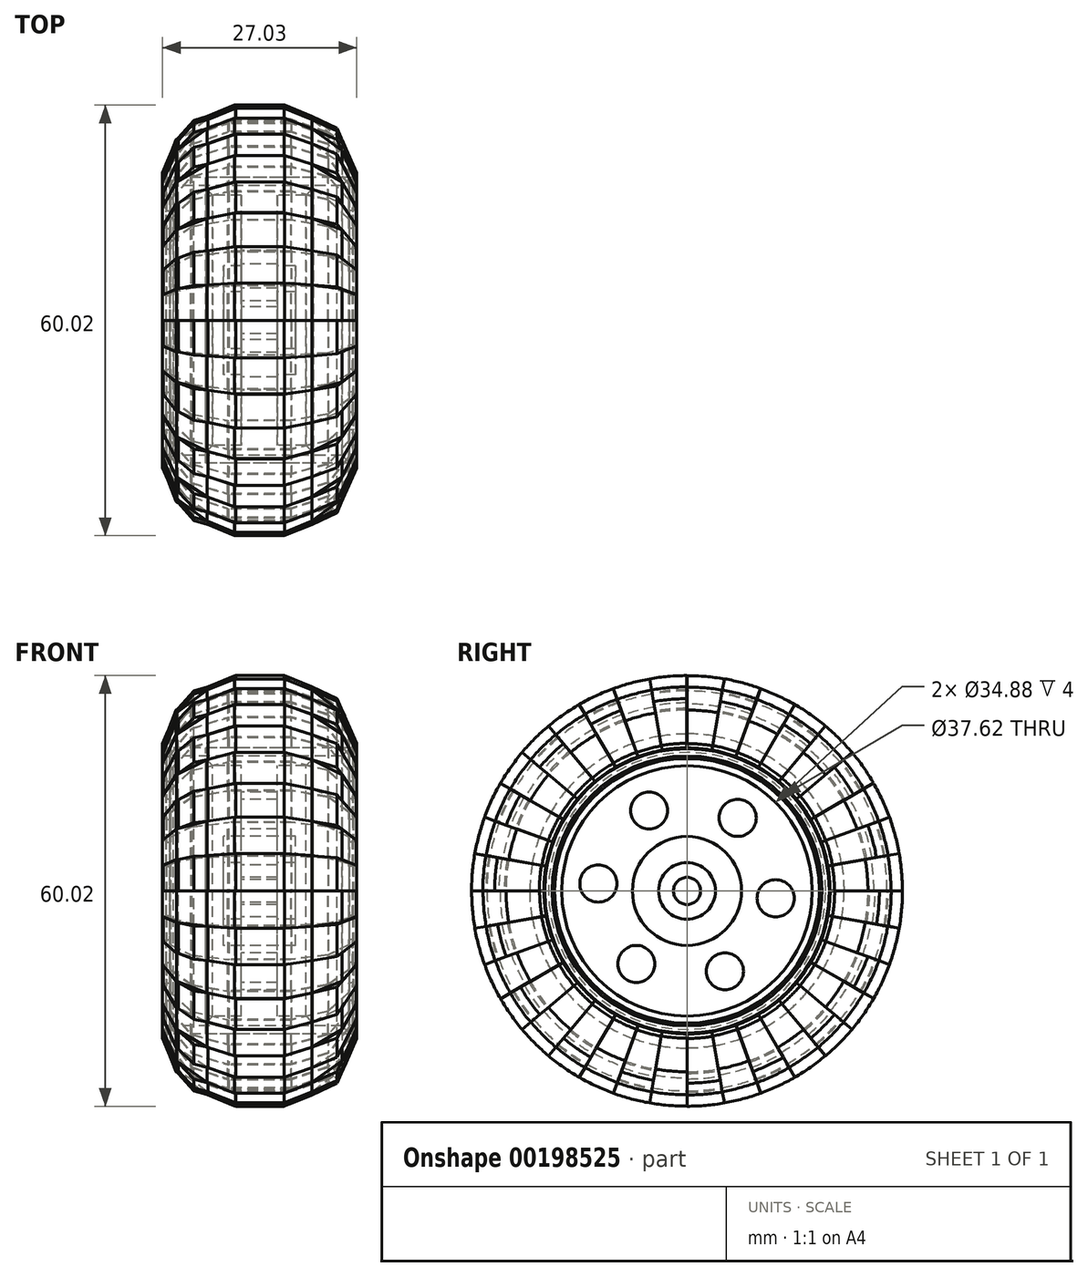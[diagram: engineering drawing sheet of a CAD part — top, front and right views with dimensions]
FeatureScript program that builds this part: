
annotation { "Feature Type Name" : "Feature", "Feature Type Description" : "" }
export const myFeature = defineFeature(function(context is Context, id is Id, definition is map)
    precondition{}
    {
        {
            var Q0;
            Q0=qCreatedBy(makeId("Top.planeOp"),FACE);
            var sketch = newSketch(context, id + "F0", { "sketchPlane" : qUnion([Q0])});
            skEllipse(sketch, "E0", {"center": v(0, -20) * mm, "majorRadius": 13.5 * mm, "minorRadius": 10 * mm, "majorAxis": v(1, 0), "construction": true});
            skLineSegment(sketch, "E1", {"start": v(0, 0) * mm, "end": v(0, -45.8) * mm, "construction": true});
            skLineSegment(sketch, "E2", {"start": v(-18.98, 0) * mm, "end": v(27.13, 0) * mm, "construction": true});
            skLineSegment(sketch, "E3", {"start": v(0, -30) * mm, "end": v(-3.5, -30) * mm});
            skLineSegment(sketch, "E4", {"start": v(-3.5, -30) * mm, "end": v(-7.3, -28.4) * mm});
            skLineSegment(sketch, "E5", {"start": v(-7.3, -28.4) * mm, "end": v(-11.53, -25.2) * mm});
            skLineSegment(sketch, "E6", {"start": v(-11.53, -25.2) * mm, "end": v(-11.53, -25.2) * mm});
            skLineSegment(sketch, "E7", {"start": v(-13, -20.54) * mm, "end": v(-13.01, -19.92) * mm});
            skLineSegment(sketch, "E8", {"start": v(-13.01, -19.92) * mm, "end": v(-12.45, -19.92) * mm});
            skLineSegment(sketch, "E9", {"start": v(-12.45, -19.92) * mm, "end": v(-12.45, -21.9) * mm});
            skLineSegment(sketch, "E10", {"start": v(-12.45, -21.9) * mm, "end": v(-9.59, -26.05) * mm});
            skLineSegment(sketch, "E11", {"start": v(-9.59, -26.05) * mm, "end": v(-4.45, -27.86) * mm});
            skLineSegment(sketch, "E12", {"start": v(-4.45, -27.86) * mm, "end": v(0, -27.86) * mm});
            skLineSegment(sketch, "E13", {"start": v(-11.53, -25.2) * mm, "end": v(-13.48, -20.53) * mm});
            skLineSegment(sketch, "E14", {"start": v(-13.48, -20.53) * mm, "end": v(-13, -20.54) * mm});
            skLineSegment(sketch, "E15.MirrorCS", {"start": v(13.48, -20.53) * mm, "end": v(13, -20.54) * mm});
            skLineSegment(sketch, "E16.MirrorCS", {"start": v(11.53, -25.2) * mm, "end": v(11.53, -25.2) * mm});
            skLineSegment(sketch, "E17.MirrorCS", {"start": v(3.5, -30) * mm, "end": v(7.3, -28.4) * mm});
            skLineSegment(sketch, "E18.MirrorCS", {"start": v(13.01, -19.92) * mm, "end": v(12.45, -19.92) * mm});
            skLineSegment(sketch, "E19.MirrorCS", {"start": v(4.45, -27.86) * mm, "end": v(0, -27.86) * mm});
            skLineSegment(sketch, "E20.MirrorCS", {"start": v(11.53, -25.2) * mm, "end": v(13.48, -20.53) * mm});
            skLineSegment(sketch, "E21.MirrorCS", {"start": v(9.59, -26.05) * mm, "end": v(4.45, -27.86) * mm});
            skLineSegment(sketch, "E22.MirrorCS", {"start": v(7.3, -28.4) * mm, "end": v(11.53, -25.2) * mm});
            skLineSegment(sketch, "E23.MirrorCS", {"start": v(0, -30) * mm, "end": v(3.5, -30) * mm});
            skLineSegment(sketch, "E24.MirrorCS", {"start": v(12.45, -21.9) * mm, "end": v(9.59, -26.05) * mm});
            skLineSegment(sketch, "E25.MirrorCS", {"start": v(12.45, -19.92) * mm, "end": v(12.45, -21.9) * mm});
            skLineSegment(sketch, "E26.MirrorCS", {"start": v(13, -20.54) * mm, "end": v(13.01, -19.92) * mm});
            skSolve(sketch);
        }
        {
            var Q0;
            Q0 = qSketchRegion(id + "F0", true);
            var Q1;
            Q1=sQuery(id+"F0.wireOp",EDGE,"E2");
            revolve(context, id + "F1", {"entities" : qUnion([Q0]), "axis" : qUnion([Q1]), "revolveType" : RevolveType.ONE_DIRECTION, "angle" : 10 * degree});
        }
        {
            var Q0;
            Q0=makeQuery(id+"F1.opRevolve","SWEPT_BODY",BODY,{"disambiguationData":[OSD([sQuery(id+"F0.wireOp",EDGE,"E3"),sQuery(id+"F0.wireOp",EDGE,"E4"),sQuery(id+"F0.wireOp",EDGE,"E5"),sQuery(id+"F0.wireOp",EDGE,"E6"),sQuery(id+"F0.wireOp",EDGE,"E6"),sQuery(id+"F0.wireOp",EDGE,"E6"),sQuery(id+"F0.wireOp",EDGE,"E6"),sQuery(id+"F0.wireOp",EDGE,"E7"),sQuery(id+"F0.wireOp",EDGE,"E8"),sQuery(id+"F0.wireOp",EDGE,"E9"),sQuery(id+"F0.wireOp",EDGE,"E10"),sQuery(id+"F0.wireOp",EDGE,"E11"),sQuery(id+"F0.wireOp",EDGE,"E12"),sQuery(id+"F0.wireOp",EDGE,"E13"),sQuery(id+"F0.wireOp",EDGE,"E14"),sQuery(id+"F0.wireOp",EDGE,"E15.MirrorCS"),sQuery(id+"F0.wireOp",EDGE,"E16.MirrorCS"),sQuery(id+"F0.wireOp",EDGE,"E17.MirrorCS"),sQuery(id+"F0.wireOp",EDGE,"E16.MirrorCS"),sQuery(id+"F0.wireOp",EDGE,"E16.MirrorCS"),sQuery(id+"F0.wireOp",EDGE,"E18.MirrorCS"),sQuery(id+"F0.wireOp",EDGE,"E19.MirrorCS"),sQuery(id+"F0.wireOp",EDGE,"E20.MirrorCS"),sQuery(id+"F0.wireOp",EDGE,"E21.MirrorCS"),sQuery(id+"F0.wireOp",EDGE,"E22.MirrorCS"),sQuery(id+"F0.wireOp",EDGE,"E23.MirrorCS"),sQuery(id+"F0.wireOp",EDGE,"E24.MirrorCS"),sQuery(id+"F0.wireOp",EDGE,"E25.MirrorCS"),sQuery(id+"F0.wireOp",EDGE,"E16.MirrorCS"),sQuery(id+"F0.wireOp",EDGE,"E26.MirrorCS")])]});
            var Q1;
            Q1=sQuery(id+"F0.wireOp",EDGE,"E2");
            circularPattern(context, id + "F2", {"entities" : qUnion([Q0]), "axis" : qUnion([Q1]), "angle" : 360 * degree, "instanceCount" : 18, "equalSpace" : true});
        }
        {
            var Q0;
            Q0=qCreatedBy(makeId("Top.planeOp"),FACE);
            var sketch = newSketch(context, id + "F3", { "sketchPlane" : qUnion([Q0])});
            skEllipse(sketch, "E27", {"center": v(0.07, -20.01) * mm, "majorRadius": 13.5 * mm, "minorRadius": 10 * mm, "majorAxis": v(1, 0), "construction": true});
            skLineSegment(sketch, "E28", {"start": v(0.07, -0.01) * mm, "end": v(0.07, -51.08) * mm, "construction": true});
            skLineSegment(sketch, "E29", {"start": v(-18.86, -0.14) * mm, "end": v(27.25, -0.14) * mm, "construction": true});
            skLineSegment(sketch, "E30", {"start": v(0.07, -30.01) * mm, "end": v(-3.31, -30.01) * mm});
            skLineSegment(sketch, "E31", {"start": v(-3.31, -30.01) * mm, "end": v(-7.2, -28.44) * mm});
            skLineSegment(sketch, "E32", {"start": v(-11.27, -25.44) * mm, "end": v(-11.27, -25.44) * mm});
            skLineSegment(sketch, "E33", {"start": v(-12.93, -20.57) * mm, "end": v(-12.95, -19.93) * mm});
            skLineSegment(sketch, "E34", {"start": v(-12.95, -19.93) * mm, "end": v(-12.4, -19.93) * mm});
            skLineSegment(sketch, "E35", {"start": v(-12.4, -19.93) * mm, "end": v(-12.4, -21.88) * mm});
            skLineSegment(sketch, "E36", {"start": v(-12.4, -21.88) * mm, "end": v(-9.4, -26.2) * mm});
            skLineSegment(sketch, "E37", {"start": v(-9.4, -26.2) * mm, "end": v(-4.26, -28.02) * mm});
            skLineSegment(sketch, "E38", {"start": v(-4.26, -28.02) * mm, "end": v(0.12, -28.02) * mm});
            skLineSegment(sketch, "E39.MirrorCS", {"start": v(11.4, -25.44) * mm, "end": v(11.4, -25.44) * mm});
            skLineSegment(sketch, "E40.MirrorCS", {"start": v(3.45, -30.01) * mm, "end": v(7.33, -28.44) * mm});
            skLineSegment(sketch, "E41.MirrorCS", {"start": v(13.1, -19.93) * mm, "end": v(12.53, -19.93) * mm});
            skLineSegment(sketch, "E42.MirrorCS", {"start": v(4.4, -28.02) * mm, "end": v(0.02, -28.02) * mm});
            skLineSegment(sketch, "E43.MirrorCS", {"start": v(9.54, -26.2) * mm, "end": v(4.4, -28.02) * mm});
            skLineSegment(sketch, "E44.MirrorCS", {"start": v(0.07, -30.01) * mm, "end": v(3.45, -30.01) * mm});
            skLineSegment(sketch, "E45.MirrorCS", {"start": v(12.53, -21.88) * mm, "end": v(9.54, -26.2) * mm});
            skLineSegment(sketch, "E46.MirrorCS", {"start": v(12.53, -19.93) * mm, "end": v(12.53, -21.88) * mm});
            skLineSegment(sketch, "E47.MirrorCS", {"start": v(13.07, -20.57) * mm, "end": v(13.1, -19.93) * mm});
            skPoint(sketch, "E48.MirrorCS.end.orphan", {"position": v(-11.27, -25.44) * mm});
            skLineSegment(sketch, "E49", {"start": v(-11.27, -25.44) * mm, "end": v(-9.14, -27.88) * mm});
            skLineSegment(sketch, "E50", {"start": v(-9.14, -27.88) * mm, "end": v(-7.2, -28.44) * mm});
            skPoint(sketch, "E51.MirrorCS.end.orphan", {"position": v(11.4, -25.44) * mm});
            skLineSegment(sketch, "E52", {"start": v(7.33, -28.44) * mm, "end": v(10.82, -26.8) * mm});
            skLineSegment(sketch, "E53", {"start": v(10.82, -26.8) * mm, "end": v(11.4, -25.44) * mm});
            skPoint(sketch, "E54.MirrorCS.start.orphan", {"position": v(13.57, -20.26) * mm});
            skLineSegment(sketch, "E55", {"start": v(13.07, -20.57) * mm, "end": v(13.55, -20.57) * mm});
            skLineSegment(sketch, "E56", {"start": v(13.55, -20.57) * mm, "end": v(11.4, -25.44) * mm});
            skPoint(sketch, "E57.MirrorCS.end.orphan", {"position": v(-13.43, -20.26) * mm});
            skLineSegment(sketch, "E58", {"start": v(-12.93, -20.57) * mm, "end": v(-13.4, -20.57) * mm});
            skLineSegment(sketch, "E59", {"start": v(-13.4, -20.57) * mm, "end": v(-11.62, -25.21) * mm});
            skLineSegment(sketch, "E60", {"start": v(-11.62, -25.21) * mm, "end": v(-11.27, -25.44) * mm});
            skLineSegment(sketch, "E61", {"start": v(-18.86, -0.14) * mm, "end": v(-39.36, 0) * mm, "construction": true});
            skSolve(sketch);
        }
        {
            var Q0;
            Q0=makeQuery(id+"F3.imprint","IMPRINT",FACE,{"disambiguationData":[TD([[makeQuery(id+"F3.imprint","IMPRINT",EDGE,{"derivedFrom":sQuery(id+"F3.wireOp",EDGE,"E47.MirrorCS")}),1.0]])]});
            var Q1;
            Q1=sQuery(id+"F3.wireOp",EDGE,"E29");
            revolve(context, id + "F4", {"entities" : qUnion([Q0]), "axis" : qUnion([Q1]), "revolveType" : RevolveType.ONE_DIRECTION, "oppositeDirection" : true, "angle" : 10 * degree});
        }
        {
            var Q0;
            Q0=makeQuery(id+"F4.opRevolve","SWEPT_BODY",BODY,{"disambiguationData":[OSD([sQuery(id+"F3.wireOp",EDGE,"E47.MirrorCS"),sQuery(id+"F3.wireOp",EDGE,"E34"),sQuery(id+"F3.wireOp",EDGE,"E33"),sQuery(id+"F3.wireOp",EDGE,"E41.MirrorCS"),sQuery(id+"F3.wireOp",EDGE,"E45.MirrorCS"),sQuery(id+"F3.wireOp",EDGE,"E37"),sQuery(id+"F3.wireOp",EDGE,"E35"),sQuery(id+"F3.wireOp",EDGE,"E46.MirrorCS"),sQuery(id+"F3.wireOp",EDGE,"E38"),sQuery(id+"F3.wireOp",EDGE,"E36"),sQuery(id+"F3.wireOp",EDGE,"E42.MirrorCS"),sQuery(id+"F3.wireOp",EDGE,"E40.MirrorCS"),sQuery(id+"F3.wireOp",EDGE,"E44.MirrorCS"),sQuery(id+"F3.wireOp",EDGE,"E30"),sQuery(id+"F3.wireOp",EDGE,"E31"),sQuery(id+"F3.wireOp",EDGE,"E43.MirrorCS"),sQuery(id+"F3.wireOp",EDGE,"E49"),sQuery(id+"F3.wireOp",EDGE,"E50"),sQuery(id+"F3.wireOp",EDGE,"E52"),sQuery(id+"F3.wireOp",EDGE,"E53"),sQuery(id+"F3.wireOp",EDGE,"E55"),sQuery(id+"F3.wireOp",EDGE,"E56"),sQuery(id+"F3.wireOp",EDGE,"E58"),sQuery(id+"F3.wireOp",EDGE,"E59"),sQuery(id+"F3.wireOp",EDGE,"E60")])]});
            var Q1;
            Q1=sQuery(id+"F0.wireOp",EDGE,"E2");
            circularPattern(context, id + "F5", {"entities" : qUnion([Q0]), "axis" : qUnion([Q1]), "angle" : 360 * degree, "instanceCount" : 18, "equalSpace" : true});
        }
        {
            var Q0;
            Q0=qCreatedBy(makeId("Right.planeOp"),FACE);
            var sketch = newSketch(context, id + "F6", { "sketchPlane" : qUnion([Q0])});
            skCircle(sketch, "E62", {"center": v(0, 0) * mm, "radius": 19.92 * mm});
            skCircle(sketch, "E63", {"center": v(0, 0) * mm, "radius": 18.8 * mm});
            skCircle(sketch, "E64", {"center": v(0, 0) * mm, "radius": 17.44 * mm});
            skCircle(sketch, "E65", {"center": v(0, 0) * mm, "radius": 7.6 * mm});
            skCircle(sketch, "E66", {"center": v(0, 0) * mm, "radius": 3.95 * mm});
            skCircle(sketch, "E67", {"center": v(0, 0) * mm, "radius": 1.88 * mm});
            skLineSegment(sketch, "E68", {"start": v(-9.58, -14.57) * mm, "end": v(9.88, 14.37) * mm, "construction": true});
            skCircle(sketch, "E69.3.0", {"center": v(7.06, 10.18) * mm, "radius": 2.59 * mm});
            skPoint(sketch, "E69.center", {"position": v(-0.12, -0.24) * mm});
            skCircle(sketch, "E70.1.0", {"center": v(-5.29, 11.2) * mm, "radius": 2.59 * mm});
            skCircle(sketch, "E70.2.0", {"center": v(-12.35, 1.02) * mm, "radius": 2.59 * mm});
            skCircle(sketch, "E70.3.0", {"center": v(-7.06, -10.18) * mm, "radius": 2.59 * mm});
            skCircle(sketch, "E70.4.0", {"center": v(5.29, -11.2) * mm, "radius": 2.59 * mm});
            skCircle(sketch, "E70.5.0", {"center": v(12.35, -1.02) * mm, "radius": 2.59 * mm});
            skSolve(sketch);
        }
        {
            var Q0;
            Q0=makeQuery(id+"F6.imprint","IMPRINT",FACE,{"disambiguationData":[TD([[makeQuery(id+"F6.imprint","IMPRINT",EDGE,{"derivedFrom":sQuery(id+"F6.wireOp",EDGE,"E62")}),1.0]])]});
            extrude(context, id + "F7", {"entities" : qUnion([Q0]), "endBound" : BoundingType.SYMMETRIC, "depth" : 25 * mm});
        }
        {
            var Q0;
            Q0 = qSketchRegion(id + "F6", true);
            var Q1;
            Q1=makeQuery(id+"F6.imprint","IMPRINT",FACE,{"disambiguationData":[TD([[makeQuery(id+"F6.imprint","IMPRINT",EDGE,{"derivedFrom":sQuery(id+"F6.wireOp",EDGE,"E63")}),1.0]])]});
            extrude(context, id + "F8", {"entities" : qUnion([Q0, Q1]), "endBound" : BoundingType.SYMMETRIC, "depth" : 15 * mm});
        }
        {
            var Q0;
            Q0=makeQuery(id+"F6.imprint","IMPRINT",FACE,{"disambiguationData":[TD([[makeQuery(id+"F6.imprint","IMPRINT",EDGE,{"derivedFrom":sQuery(id+"F6.wireOp",EDGE,"E64")}),1.0]])]});
            extrude(context, id + "F9", {"entities" : qUnion([Q0]), "operationType" : NewBodyOperationType.ADD, "endBound" : BoundingType.SYMMETRIC, "depth" : 5 * mm});
        }
        {
            var Q0;
            Q0=makeQuery(id+"F6.imprint","IMPRINT",FACE,{"disambiguationData":[TD([[makeQuery(id+"F6.imprint","IMPRINT",EDGE,{"derivedFrom":sQuery(id+"F6.wireOp",EDGE,"E65")}),1.0]])]});
            extrude(context, id + "F10", {"entities" : qUnion([Q0]), "operationType" : NewBodyOperationType.ADD, "endBound" : BoundingType.SYMMETRIC, "depth" : 10 * mm});
        }
        {
            var Q0;
            Q0=makeQuery(id+"F6.imprint","IMPRINT",FACE,{"disambiguationData":[TD([[makeQuery(id+"F6.imprint","IMPRINT",EDGE,{"derivedFrom":sQuery(id+"F6.wireOp",EDGE,"E66")}),1.0]])]});
            extrude(context, id + "F11", {"entities" : qUnion([Q0]), "operationType" : NewBodyOperationType.ADD, "endBound" : BoundingType.SYMMETRIC, "depth" : 5 * mm});
        }
        {
            var Q0;
            Q0=makeQuery(id+"F7.opExtrude","CAP_EDGE",EDGE,{"disambiguationData":[OSD([sQuery(id+"F6.wireOp",EDGE,"E63")])],"isStart":true});
            chamfer(context, id + "F12", {"entities" : qUnion([Q0]), "width" : 0.5 * mm, "tangentPropagation" : true});
        }
        {
            var Q0;
            Q0=makeQuery(id+"F8.opExtrude","CAP_EDGE",EDGE,{"disambiguationData":[OSD([sQuery(id+"F6.wireOp",EDGE,"E64")])],"isStart":true});
            chamfer(context, id + "F13", {"entities" : qUnion([Q0]), "width" : 1 * mm, "tangentPropagation" : true});
        }
        {
            var Q0;
            Q0=makeQuery(id+"F8.opExtrude","CAP_EDGE",EDGE,{"disambiguationData":[OSD([sQuery(id+"F6.wireOp",EDGE,"E64")])],"isStart":false});
            var Q1;
            Q1=makeQuery(id+"F7.opExtrude","CAP_EDGE",EDGE,{"disambiguationData":[OSD([sQuery(id+"F6.wireOp",EDGE,"E63")])],"isStart":false});
            chamfer(context, id + "F14", {"entities" : qUnion([Q0, Q1]), "width" : 1 * mm, "tangentPropagation" : true});
        }
    });
